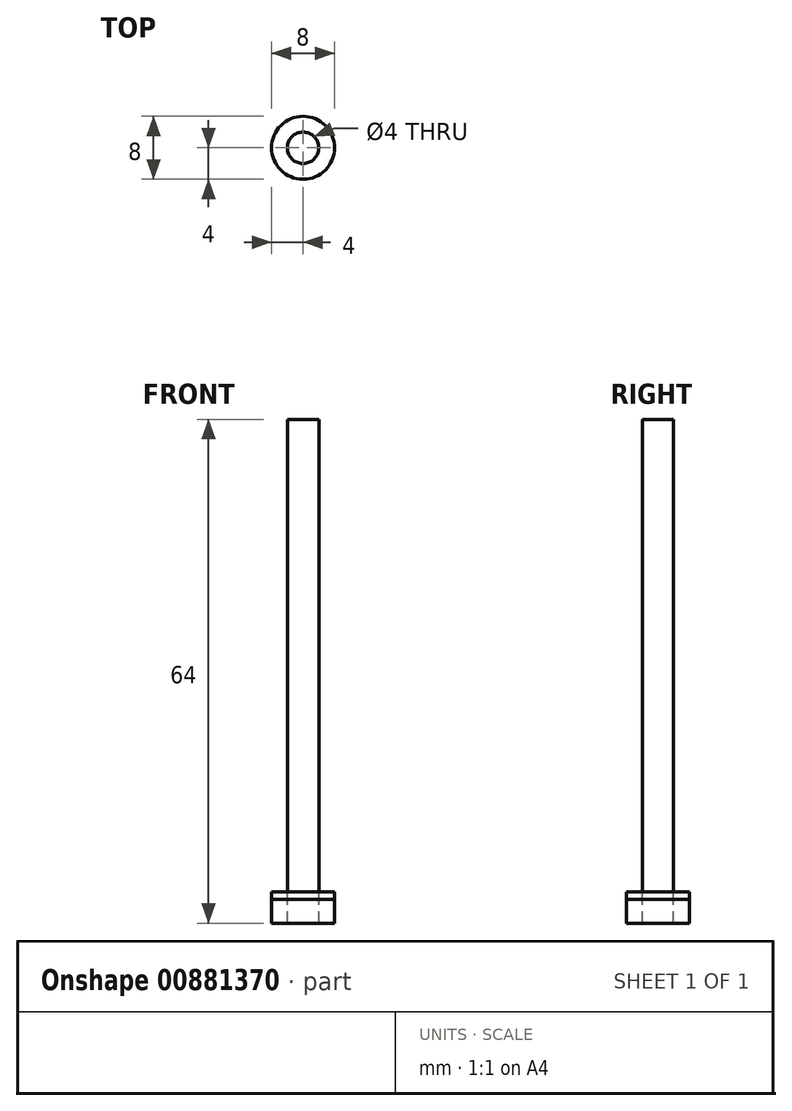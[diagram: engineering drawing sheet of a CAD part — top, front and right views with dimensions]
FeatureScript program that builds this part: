
annotation { "Feature Type Name" : "Feature", "Feature Type Description" : "" }
export const myFeature = defineFeature(function(context is Context, id is Id, definition is map)
    precondition{}
    {
        {
            var Q0;
            Q0=qCreatedBy(makeId("Top.planeOp"),FACE);
            var sketch = newSketch(context, id + "F0", { "sketchPlane" : qUnion([Q0])});
            skCircle(sketch, "E0", {"center": v(0, 0) * mm, "radius": 4 * mm});
            skCircle(sketch, "E1", {"center": v(0, 0) * mm, "radius": 2 * mm});
            skSolve(sketch);
        }
        {
            var Q0;
            Q0=makeQuery(id+"F0.imprint","IMPRINT",FACE,{"disambiguationData":[TD([[makeQuery(id+"F0.imprint","IMPRINT",EDGE,{"derivedFrom":sQuery(id+"F0.wireOp",EDGE,"E0")}),1.0]])]});
            extrude(context, id + "F1", {"entities" : qUnion([Q0]), "oppositeDirection" : true, "depth" : 4 * mm, "offsetDistance" : 25 * mm});
        }
        {
            var Q0;
            Q0=makeQuery(id+"F0.imprint","IMPRINT",FACE,{"disambiguationData":[TD([[makeQuery(id+"F0.imprint","IMPRINT",EDGE,{"derivedFrom":sQuery(id+"F0.wireOp",EDGE,"E1")}),1.0]])]});
            extrude(context, id + "F2", {"entities" : qUnion([Q0]), "depth" : 60 * mm, "offsetDistance" : 25 * mm});
        }
        {
            var Q0;
            Q0=makeQuery(id+"F0.imprint","IMPRINT",FACE,{"disambiguationData":[TD([[makeQuery(id+"F0.imprint","IMPRINT",EDGE,{"derivedFrom":sQuery(id+"F0.wireOp",EDGE,"E0")}),1.0]])]});
            var Q1;
            Q1=makeQuery(id+"F0.imprint","IMPRINT",FACE,{"disambiguationData":[TD([[makeQuery(id+"F0.imprint","IMPRINT",EDGE,{"derivedFrom":sQuery(id+"F0.wireOp",EDGE,"E1")}),1.0]])]});
            extrude(context, id + "F3", {"entities" : qUnion([Q0, Q1]), "oppositeDirection" : true, "depth" : 1 * mm, "offsetDistance" : 25 * mm});
        }
    });
